# Revit family: ACE-B
name_source: partatom
category: Mechanical Equipment
units: mm (PartAtom-declared; Revit-internal decimal feet)

## family parameters
Always vertical = Yes
Cut with Voids When Loaded = No
Part Type = Normal
Room Calculation Point = No
Round Connector Dimension = Use Diameter
Shared = No
Work Plane-Based = No

## types (21) — shared parameters
2" = 0' - 2"
Model = ACEB
ONE EIGTH = 0' - 0 1/8"
Type Comments = Downblast Centrifugal Exhaust Ventilator Roof Mounted/Belt Drive
URL = www.lorencook.com
ZERO = 0' - 0"

## per-type parameters (varying)
| type | -CURB_FLANGE/2 | -CURB_OD/2 | -RO/2 | APLUSG | A_SUB | B_SUB | CURB_FLANGE | CURB_FLANGE/2 | CURB_OD | CURB_OD/2 | C_SUB | DEPTH | EDGE_TO_CURB | EIGHTH_T_SQ | HALF_B_SUB | Manufacturer | RO/2 | ROOF_OPENING | T_SQ | T_SQ_HALF |
| 60_ACE-B | -0' - 10 1/4" | -0' - 8 1/4" | -0' - 6 3/4" | 0' - 4 7/8" | 0' - 2 7/8" | 1' - 11 9/16" | 1' - 8 1/2" | 0' - 10 1/4" | 1' - 4 1/2" | 0' - 8 1/4" | 1' - 9 1/8" | 0' - 2" | 1' - 0 3/8" | 0' - 1 13/16" | 0' - 11 25/32" | Loren Cook Company | 0' - 6 3/4" | 1' - 1 1/2" | 1' - 6" | 0' - 9" |
| 70_ACE-B | -0' - 10 1/4" | -0' - 8 1/4" | -0' - 6 3/4" | 0' - 4 7/8" | 0' - 2 7/8" | 1' - 11 9/16" | 1' - 8 1/2" | 0' - 10 1/4" | 1' - 4 1/2" | 0' - 8 1/4" | 1' - 9 1/8" | 0' - 2" | 1' - 0 3/8" | 0' - 1 13/16" | 0' - 11 25/32" | Loren Cook Company
Loren Cook Company | 0' - 6 3/4" | 1' - 1 1/2" | 1' - 6" | 0' - 9" |
| 80_ACE-B | -0' - 10 1/4" | -0' - 8 1/4" | -0' - 6 3/4" | 0' - 4 7/8" | 0' - 2 7/8" | 1' - 11 9/16" | 1' - 8 1/2" | 0' - 10 1/4" | 1' - 4 1/2" | 0' - 8 1/4" | 1' - 9 1/8" | 0' - 2" | 1' - 0 3/8" | 0' - 1 13/16" | 0' - 11 25/32" | Loren Cook Company | 0' - 6 3/4" | 1' - 1 1/2" | 1' - 6" | 0' - 9" |
| 100_ACE-B | -0' - 10 1/4" | -0' - 8 1/4" | -0' - 6 3/4" | 0' - 4 7/8" | 0' - 2 7/8" | 1' - 11 9/16" | 1' - 8 1/2" | 0' - 10 1/4" | 1' - 4 1/2" | 0' - 8 1/4" | 1' - 9 1/8" | 0' - 2" | 0' - 2 1/4" | 0' - 1 13/16" | 0' - 11 25/32" | Loren Cook Company | 0' - 6 3/4" | 1' - 1 1/2" | 1' - 6" | 0' - 9" |
| 120_ACE-B | -0' - 11 1/4" | -0' - 9 1/4" | -0' - 7 3/4" | 0' - 3 13/16" | 0' - 1 13/16" | 2' - 4 7/16" | 1' - 10 1/2" | 0' - 11 1/4" | 1' - 6 1/2" | 0' - 9 1/4" | 2' - 2 7/8" | 0' - 2" | 1' - 0 3/8" | 0' - 2" | 1' - 2 7/32" | Loren Cook Company | 0' - 7 3/4" | 1' - 3 1/2" | 1' - 8" | 0' - 10" |
| 135_ACE-B | -0' - 11 1/4" | -0' - 9 1/4" | -0' - 7 3/4" | 0' - 4 3/16" | 0' - 2 3/16" | 2' - 4 7/16" | 1' - 10 1/2" | 0' - 11 1/4" | 1' - 6 1/2" | 0' - 9 1/4" | 2' - 3 1/4" | 0' - 2" | 1' - 0 3/8" | 0' - 2" | 1' - 2 7/32" | Loren Cook Company | 0' - 7 3/4" | 1' - 3 1/2" | 1' - 8" | 0' - 10" |
| 150_ACE-B | -1' - 1 1/4" | -0' - 11 1/4" | -0' - 9 3/4" | 0' - 5 1/16" | 0' - 3 1/16" | 2' - 8 7/8" | 2' - 2 1/2" | 1' - 1 1/4" | 1' - 10 1/2" | 0' - 11 1/4" | 2' - 4 7/8" | 0' - 2" | 1' - 0 3/8" | 0' - 2 13/32" | 1' - 4 7/16" | Loren Cook Company | 0' - 9 3/4" | 1' - 7 1/2" | 2' - 0" | 1' - 0" |
| 165_ACE-B | -1' - 1 1/4" | -0' - 11 1/4" | -0' - 9 3/4" | 0' - 5 9/16" | 0' - 3 9/16" | 2' - 8 7/8" | 2' - 2 1/2" | 1' - 1 1/4" | 1' - 10 1/2" | 0' - 11 1/4" | 2' - 5 3/8" | 0' - 2" | 1' - 0 3/8" | 0' - 2 13/32" | 1' - 4 7/16" | Loren Cook Company | 0' - 9 3/4" | 1' - 7 1/2" | 2' - 0" | 1' - 0" |
| 180_ACE-B | -1' - 4 1/4" | -1' - 2 1/4" | -1' - 0 3/4" | 0' - 6 15/16" | 0' - 3 15/16" | 3' - 1 11/16" | 2' - 8 1/2" | 1' - 4 1/4" | 2' - 4 1/2" | 1' - 2 1/4" | 2' - 10 1/2" | 0' - 3" | 1' - 0 3/8" | 0' - 3" | 1' - 6 27/32" | Loren Cook Company | 1' - 0 3/4" | 2' - 1 1/2" | 2' - 6" | 1' - 3" |
| 195_ACE-B | -1' - 4 1/4" | -1' - 2 1/4" | -1' - 0 3/4" | 0' - 7 7/16" | 0' - 4 7/16" | 3' - 1 11/16" | 2' - 8 1/2" | 1' - 4 1/4" | 2' - 4 1/2" | 1' - 2 1/4" | 2' - 11" | 0' - 3" | 1' - 0 3/8" | 0' - 3" | 1' - 6 27/32" | Loren Cook Company | 1' - 0 3/4" | 2' - 1 1/2" | 2' - 6" | 1' - 3" |
| 210_ACE-B | -1' - 4 1/4" | -1' - 2 1/4" | -1' - 0 3/4" | 0' - 7 3/4" | 0' - 4 3/4" | 3' - 7 5/8" | 2' - 8 1/2" | 1' - 4 1/4" | 2' - 4 1/2" | 1' - 2 1/4" | 3' - 1 1/4" | 0' - 3" | 1' - 0 3/8" | 0' - 3" | 1' - 9 13/16" | Loren Cook Company | 1' - 0 3/4" | 2' - 1 1/2" | 2' - 6" | 1' - 3" |
| 225_ACE-B | -1' - 4 1/4" | -1' - 2 1/4" | -1' - 0 3/4" | 0' - 7 7/8" | 0' - 4 7/8" | 3' - 7 5/8" | 2' - 8 1/2" | 1' - 4 1/4" | 2' - 4 1/2" | 1' - 2 1/4" | 3' - 1 3/8" | 0' - 3" | 1' - 0 3/8" | 0' - 3" | 1' - 9 13/16" | Loren Cook Company
Loren Cook Company | 1' - 0 3/4" | 2' - 1 1/2" | 2' - 6" | 1' - 3" |
| 245_ACE-B | -1' - 4 1/4" | -1' - 2 1/4" | -1' - 0 3/4" | 0' - 9 1/8" | 0' - 6 1/8" | 3' - 11 5/8" | 2' - 8 1/2" | 1' - 4 1/4" | 2' - 4 1/2" | 1' - 2 1/4" | 3' - 3 7/8" | 0' - 3" | 1' - 0 3/8" | 0' - 3" | 1' - 11 13/16" | Loren Cook Company | 1' - 0 3/4" | 2' - 1 1/2" | 2' - 6" | 1' - 3" |
| 270_ACE-B | -1' - 7 1/4" | -1' - 5 1/4" | -1' - 3 3/4" | 0' - 9 1/8" | 0' - 6 1/8" | 3' - 11 5/8" | 3' - 2 1/2" | 1' - 7 1/4" | 2' - 10 1/2" | 1' - 5 1/4" | 3' - 3 7/8" | 0' - 3" | 1' - 0 3/8" | 0' - 3 19/32" | 1' - 11 13/16" | Loren Cook Company | 1' - 3 3/4" | 2' - 7 1/2" | 3' - 0" | 1' - 6" |
| 300_ACE-B | -1' - 7 1/4" | -1' - 5 1/4" | -1' - 3 3/4" | 0' - 10 1/16" | 0' - 7 1/16" | 4' - 4 5/8" | 3' - 2 1/2" | 1' - 7 1/4" | 2' - 10 1/2" | 1' - 5 1/4" | 4' - 1 1/16" | 0' - 3" | 1' - 0 3/8" | 0' - 3 19/32" | 2' - 2 5/16" | Loren Cook Company | 1' - 3 3/4" | 2' - 7 1/2" | 3' - 0" | 1' - 6" |
| 330_ACE-B | -1' - 10 1/4" | -1' - 8 1/4" | -1' - 6 3/4" | 0' - 10 5/16" | 0' - 7 5/16" | 4' - 4 5/8" | 3' - 8 1/2" | 1' - 10 1/4" | 3' - 4 1/2" | 1' - 8 1/4" | 4' - 1 5/16" | 0' - 3" | 1' - 0 3/8" | 0' - 4 3/16" | 2' - 2 5/16" | Loren Cook Company | 1' - 6 3/4" | 3' - 1 1/2" | 3' - 6" | 1' - 9" |
| 365_ACE-B | -1' - 10 1/4" | -1' - 8 1/4" | -1' - 6 3/4" | 0' - 11 1/16" | 0' - 8 1/16" | 5' - 2 5/8" | 3' - 8 1/2" | 1' - 10 1/4" | 3' - 4 1/2" | 1' - 8 1/4" | 4' - 3 9/16" | 0' - 3" | 1' - 0 3/8" | 0' - 4 3/16" | 2' - 7 5/16" | Loren Cook Company | 1' - 6 3/4" | 3' - 1 1/2" | 3' - 6" | 1' - 9" |
| 402_ACE-B | -2' - 1 1/4" | -1' - 11 1/4" | -1' - 9 3/4" | 1' - 1 1/16" | 0' - 10 1/16" | 5' - 2 5/8" | 4' - 2 1/2" | 2' - 1 1/4" | 3' - 10 1/2" | 1' - 11 1/4" | 4' - 5 9/16" | 0' - 3" | 1' - 0 3/8" | 0' - 4 13/16" | 2' - 7 5/16" | Loren Cook Company | 1' - 9 3/4" | 3' - 7 1/2" | 4' - 0" | 2' - 0" |
| 445_ACE-B | -2' - 4 1/4" | -2' - 2 1/4" | -2' - 0 3/4" | 1' - 0 3/4" | 0' - 9 3/4" | 6' - 3 3/16" | 4' - 8 1/2" | 2' - 4 1/4" | 4' - 4 1/2" | 2' - 2 1/4" | 4' - 9 1/16" | 0' - 3" | 1' - 0 3/8" | 0' - 5 13/32" | 3' - 1 19/32" | Loren Cook Company | 2' - 0 3/4" | 4' - 1 1/2" | 4' - 6" | 2' - 3" |
| 490_ACE-B | -2' - 4 1/4" | -2' - 2 1/4" | -2' - 0 3/4" | 1' - 2 1/2" | 0' - 11 1/2" | 6' - 3 3/16" | 4' - 8 1/2" | 2' - 4 1/4" | 4' - 4 1/2" | 2' - 2 1/4" | 4' - 10 13/16" | 0' - 3" | 1' - 0 3/8" | 0' - 5 13/32" | 3' - 1 19/32" | Loren Cook Company | 2' - 0 3/4" | 4' - 1 1/2" | 4' - 6" | 2' - 3" |
| 540_ACE-B | -2' - 10 1/4" | -2' - 8 1/4" | -2' - 6 3/4" | 1' - 3 1/2" | 1' - 0 1/2" | 6' - 9 15/16" | 5' - 8 1/2" | 2' - 10 1/4" | 5' - 4 1/2" | 2' - 8 1/4" | 5' - 0 5/16" | 0' - 3" | 0' - 2 1/4" | 0' - 6 19/32" | 3' - 4 31/32" | Loren Cook Company | 2' - 6 3/4" | 5' - 1 1/2" | 5' - 6" | 2' - 9" |

## geometry (parser evidence)
native form markers: Sweep x1
no freeform markers — native parametric forms only
